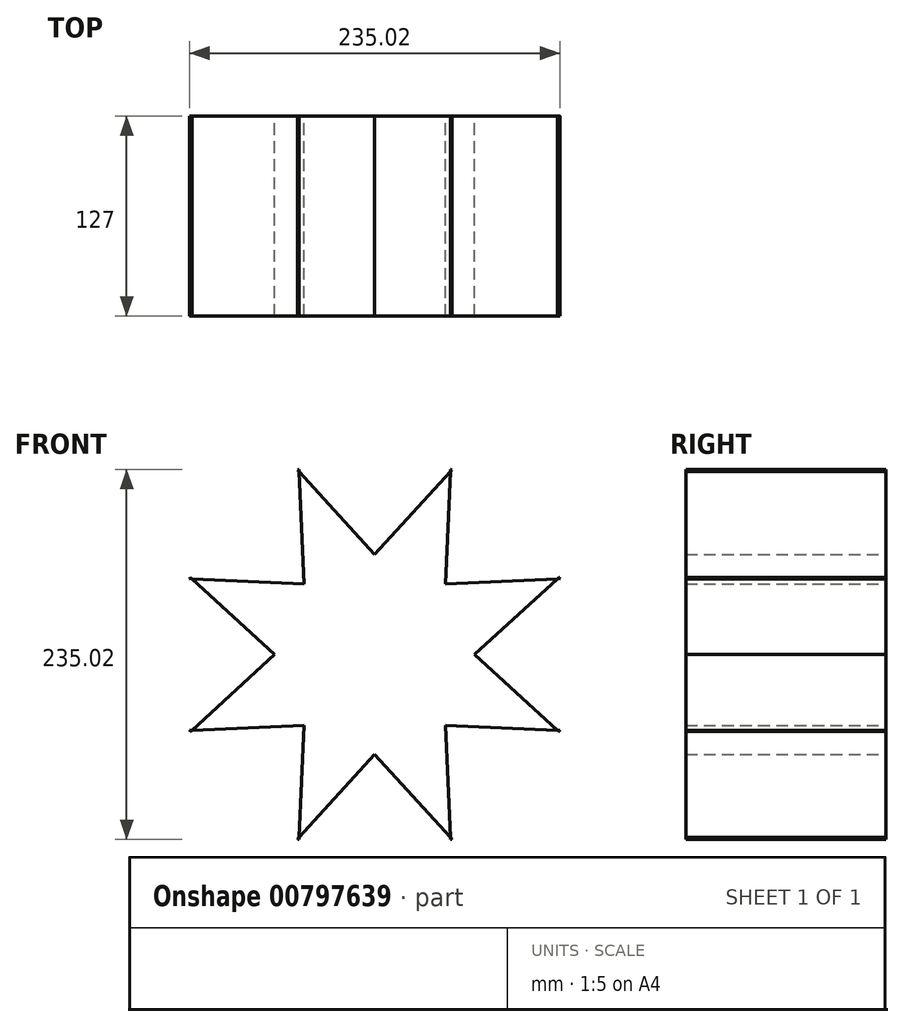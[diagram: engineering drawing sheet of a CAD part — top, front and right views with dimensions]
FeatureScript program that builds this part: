
annotation { "Feature Type Name" : "Feature", "Feature Type Description" : "" }
export const myFeature = defineFeature(function(context is Context, id is Id, definition is map)
    precondition{}
    {
        {
            var Q0;
            Q0=qCreatedBy(makeId("Front.planeOp"),FACE);
            var sketch = newSketch(context, id + "F0", { "sketchPlane" : qUnion([Q0])});
            skCircle(sketch, "E0", {"center": v(0, 0) * mm, "radius": 63.5 * mm});
            skCircle(sketch, "E1", {"center": v(0, 0) * mm, "radius": 127 * mm});
            skLineSegment(sketch, "E2", {"start": v(-188.51, 0) * mm, "end": v(197.02, 0) * mm, "construction": true});
            skLineSegment(sketch, "E3", {"start": v(0, 184.78) * mm, "end": v(0, -170.95) * mm, "construction": true});
            skSolve(sketch);
        }
        {
            var Q0;
            Q0=makeQuery(id+"F0.imprint","IMPRINT",FACE,{"disambiguationData":[TD([[makeQuery(id+"F0.imprint","IMPRINT",EDGE,{"derivedFrom":sQuery(id+"F0.wireOp",EDGE,"E0")}),-1.0]])]});
            var Q1;
            Q1=makeQuery(id+"F0.imprint","IMPRINT",FACE,{"disambiguationData":[TD([[makeQuery(id+"F0.imprint","IMPRINT",EDGE,{"derivedFrom":sQuery(id+"F0.wireOp",EDGE,"E0")}),1.0]])]});
            extrude(context, id + "F1", {"entities" : qUnion([Q0, Q1]), "depth" : 127 * mm, "offsetDistance" : 25.4 * mm});
        }
        {
            var Q0;
            Q0=qCreatedBy(makeId("Front.planeOp"),FACE);
            var sketch = newSketch(context, id + "F2", { "sketchPlane" : qUnion([Q0])});
            skCircle(sketch, "E4", {"center": v(0, 0) * mm, "radius": 63.5 * mm});
            skLineSegment(sketch, "E5", {"start": v(161.4, 0) * mm, "end": v(-167.4, 0) * mm, "construction": true});
            skLineSegment(sketch, "E6", {"start": v(0, 156.23) * mm, "end": v(0, -157.42) * mm, "construction": true});
            skLineSegment(sketch, "E7", {"start": v(0, 63.5) * mm, "end": v(-49.02, 117.16) * mm});
            skLineSegment(sketch, "E8", {"start": v(0, 63.5) * mm, "end": v(49.02, 117.16) * mm});
            skArc(sketch, "E9", {"start": v(49.02, 117.16) * mm, "mid": v(0, 127) * mm, "end": v(-49.02, 117.16) * mm});
            skLineSegment(sketch, "E10.1.0", {"start": v(44.9, 44.9) * mm, "end": v(48.18, 117.5) * mm});
            skLineSegment(sketch, "E10.1.1", {"start": v(44.9, 44.9) * mm, "end": v(117.5, 48.18) * mm});
            skLineSegment(sketch, "E10.2.0", {"start": v(63.5, 0) * mm, "end": v(117.16, 49.02) * mm});
            skLineSegment(sketch, "E10.2.1", {"start": v(63.5, 0) * mm, "end": v(117.16, -49.02) * mm});
            skLineSegment(sketch, "E10.3.0", {"start": v(44.9, -44.9) * mm, "end": v(117.5, -48.18) * mm});
            skLineSegment(sketch, "E10.3.1", {"start": v(44.9, -44.9) * mm, "end": v(48.18, -117.5) * mm});
            skLineSegment(sketch, "E10.4.0", {"start": v(0, -63.5) * mm, "end": v(49.02, -117.16) * mm});
            skLineSegment(sketch, "E10.4.1", {"start": v(0, -63.5) * mm, "end": v(-49.02, -117.16) * mm});
            skLineSegment(sketch, "E10.5.0", {"start": v(-44.9, -44.9) * mm, "end": v(-48.18, -117.5) * mm});
            skLineSegment(sketch, "E10.5.1", {"start": v(-44.9, -44.9) * mm, "end": v(-117.5, -48.18) * mm});
            skLineSegment(sketch, "E10.6.0", {"start": v(-63.5, 0) * mm, "end": v(-117.16, -49.02) * mm});
            skLineSegment(sketch, "E10.6.1", {"start": v(-63.5, 0) * mm, "end": v(-117.16, 49.02) * mm});
            skLineSegment(sketch, "E10.7.0", {"start": v(-44.9, 44.9) * mm, "end": v(-117.5, 48.18) * mm});
            skLineSegment(sketch, "E10.7.1", {"start": v(-44.9, 44.9) * mm, "end": v(-48.18, 117.5) * mm});
            skLineSegment(sketch, "E10.anchor1", {"start": v(0, 0) * mm, "end": v(0, 63.5) * mm, "construction": true});
            skLineSegment(sketch, "E10.anchor2", {"start": v(0, 0) * mm, "end": v(-44.9, 44.9) * mm, "construction": true});
            skCircle(sketch, "E11", {"center": v(0, 0) * mm, "radius": 127 * mm});
            skSolve(sketch);
        }
        {
            var Q0;
            {var subQ0=sQuery(id+"F2.wireOp",EDGE,"E10.1.0");var subQ1=sQuery(id+"F2.wireOp",EDGE,"E9");var subQ2=makeQuery(id+"F2.imprint","INTERSECT",VERTEX,{"derivedFrom":[subQ1,subQ0]});Q0=makeQuery(id+"F2.imprint","IMPRINT",FACE,{"disambiguationData":[TD([[makeQuery(id+"F2.imprint","IMPRINT",EDGE,{"disambiguationData":[TD([[subQ2,-1.0]])],"derivedFrom":subQ1}),1.0]])]});}
            var Q1;
            {var subQ3=sQuery(id+"F2.wireOp",EDGE,"E10.2.0");var subQ5=sQuery(id+"F2.wireOp",EDGE,"E11");var subQ6=makeQuery(id+"F2.imprint","INTERSECT",VERTEX,{"derivedFrom":[subQ3,subQ5]});Q1=makeQuery(id+"F2.imprint","IMPRINT",FACE,{"disambiguationData":[TD([[makeQuery(id+"F2.imprint","IMPRINT",EDGE,{"disambiguationData":[TD([[subQ6,1.0]])],"derivedFrom":subQ3}),1.0]])]});}
            var Q2;
            {var subQ5=sQuery(id+"F2.wireOp",EDGE,"E11");var subQ7=sQuery(id+"F2.wireOp",EDGE,"E10.1.1");var subQ8=makeQuery(id+"F2.imprint","INTERSECT",VERTEX,{"derivedFrom":[subQ7,subQ5]});Q2=makeQuery(id+"F2.imprint","IMPRINT",FACE,{"disambiguationData":[TD([[makeQuery(id+"F2.imprint","IMPRINT",EDGE,{"disambiguationData":[TD([[subQ8,1.0]])],"derivedFrom":subQ7}),-1.0]])]});}
            var Q3;
            {var subQ5=sQuery(id+"F2.wireOp",EDGE,"E11");var subQ7=sQuery(id+"F2.wireOp",EDGE,"E10.2.1");var subQ9=makeQuery(id+"F2.imprint","INTERSECT",VERTEX,{"derivedFrom":[subQ7,subQ5]});Q3=makeQuery(id+"F2.imprint","IMPRINT",FACE,{"disambiguationData":[TD([[makeQuery(id+"F2.imprint","IMPRINT",EDGE,{"disambiguationData":[TD([[subQ9,1.0]])],"derivedFrom":subQ7}),-1.0]])]});}
            var Q4;
            {var subQ5=sQuery(id+"F2.wireOp",EDGE,"E11");var subQ7=sQuery(id+"F2.wireOp",EDGE,"E10.3.1");var subQ9=makeQuery(id+"F2.imprint","INTERSECT",VERTEX,{"derivedFrom":[subQ7,subQ5]});Q4=makeQuery(id+"F2.imprint","IMPRINT",FACE,{"disambiguationData":[TD([[makeQuery(id+"F2.imprint","IMPRINT",EDGE,{"disambiguationData":[TD([[subQ9,1.0]])],"derivedFrom":subQ7}),-1.0]])]});}
            var Q5;
            {var subQ5=sQuery(id+"F2.wireOp",EDGE,"E11");var subQ7=sQuery(id+"F2.wireOp",EDGE,"E10.4.1");var subQ9=makeQuery(id+"F2.imprint","INTERSECT",VERTEX,{"derivedFrom":[subQ7,subQ5]});Q5=makeQuery(id+"F2.imprint","IMPRINT",FACE,{"disambiguationData":[TD([[makeQuery(id+"F2.imprint","IMPRINT",EDGE,{"disambiguationData":[TD([[subQ9,1.0]])],"derivedFrom":subQ7}),-1.0]])]});}
            var Q6;
            {var subQ5=sQuery(id+"F2.wireOp",EDGE,"E11");var subQ7=sQuery(id+"F2.wireOp",EDGE,"E10.5.1");var subQ8=makeQuery(id+"F2.imprint","INTERSECT",VERTEX,{"derivedFrom":[subQ7,subQ5]});Q6=makeQuery(id+"F2.imprint","IMPRINT",FACE,{"disambiguationData":[TD([[makeQuery(id+"F2.imprint","IMPRINT",EDGE,{"disambiguationData":[TD([[subQ8,1.0]])],"derivedFrom":subQ7}),-1.0]])]});}
            var Q7;
            {var subQ5=sQuery(id+"F2.wireOp",EDGE,"E11");var subQ6=sQuery(id+"F2.wireOp",EDGE,"E10.6.1");var subQ7=makeQuery(id+"F2.imprint","INTERSECT",VERTEX,{"derivedFrom":[subQ6,subQ5]});Q7=makeQuery(id+"F2.imprint","IMPRINT",FACE,{"disambiguationData":[TD([[makeQuery(id+"F2.imprint","IMPRINT",EDGE,{"disambiguationData":[TD([[subQ7,1.0]])],"derivedFrom":subQ6}),-1.0]])]});}
            extrude(context, id + "F3", {"entities" : qUnion([Q0, Q1, Q2, Q3, Q4, Q5, Q6, Q7]), "operationType" : NewBodyOperationType.REMOVE, "endBound" : BoundingType.THROUGH_ALL, "depth" : 25.4 * mm, "offsetDistance" : 25.4 * mm});
        }
    });
